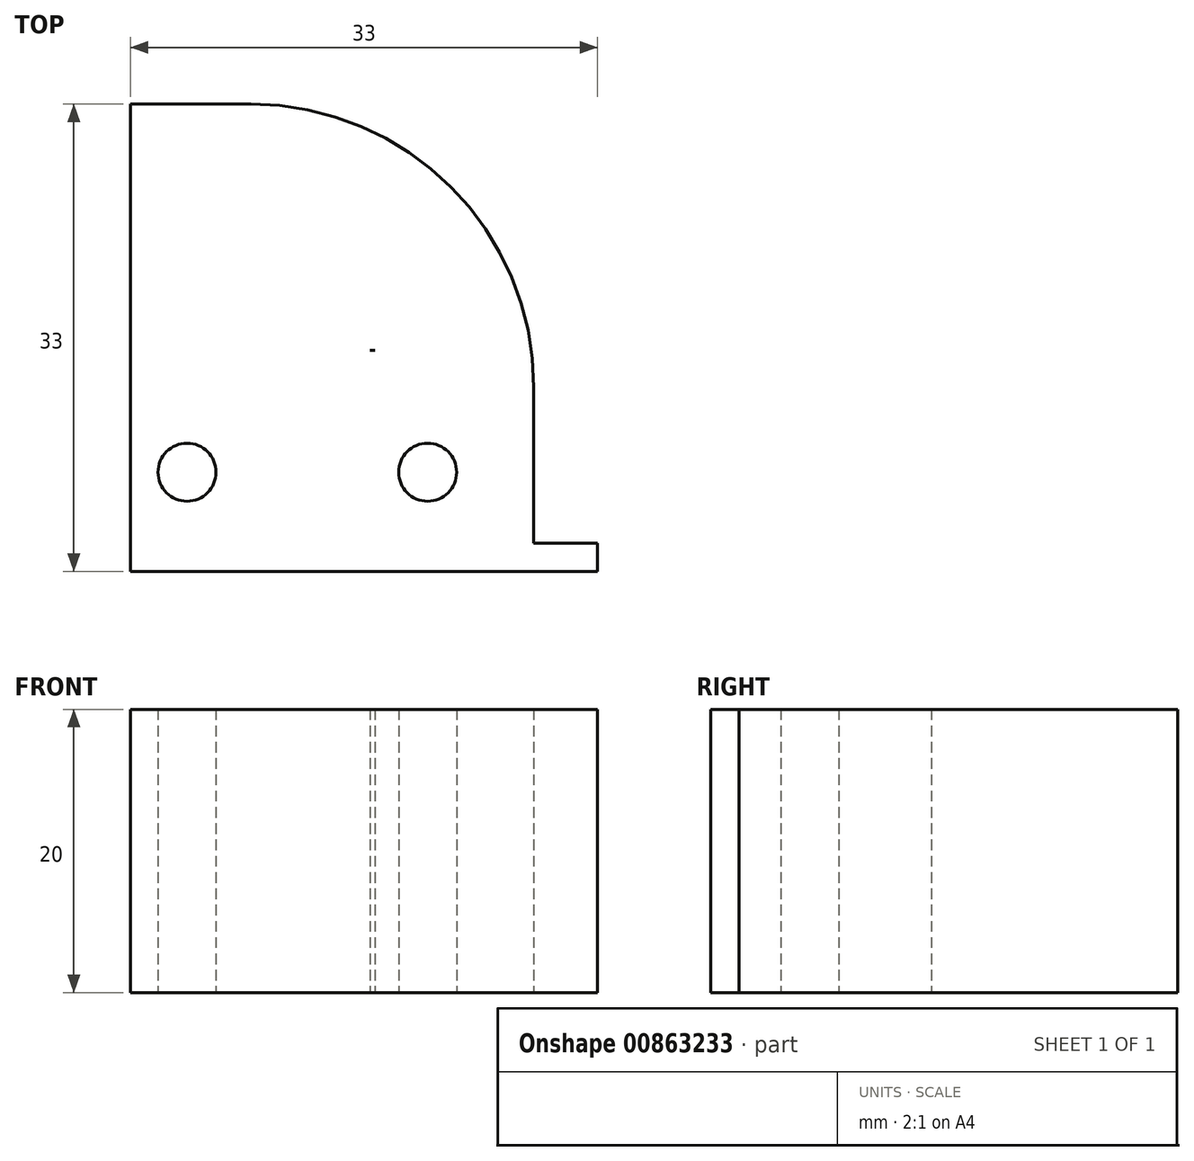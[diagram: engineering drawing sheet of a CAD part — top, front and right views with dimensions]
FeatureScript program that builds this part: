
annotation { "Feature Type Name" : "Feature", "Feature Type Description" : "" }
export const myFeature = defineFeature(function(context is Context, id is Id, definition is map)
    precondition{}
    {
        {
            var Q0;
            Q0=qCreatedBy(makeId("Top.planeOp"),FACE);
            var sketch = newSketch(context, id + "F0", { "sketchPlane" : qUnion([Q0])});
            skLineSegment(sketch, "E0.bottom", {"start": v(0, 0) * mm, "end": v(33, 0) * mm});
            skLineSegment(sketch, "E0.top", {"start": v(0, 33) * mm, "end": v(8.5, 33) * mm});
            skLineSegment(sketch, "E0.left", {"start": v(0, 0) * mm, "end": v(0, 33) * mm});
            skLineSegment(sketch, "E0.right", {"start": v(33, 0) * mm, "end": v(33, 2) * mm});
            skLineSegment(sketch, "E1", {"start": v(33, 2) * mm, "end": v(28.5, 2) * mm});
            skLineSegment(sketch, "E2", {"start": v(28.5, 2) * mm, "end": v(28.5, 13) * mm});
            skArc(sketch, "E3", {"start": v(28.5, 13) * mm, "mid": v(22.64, 27.14) * mm, "end": v(8.5, 33) * mm});
            skCircle(sketch, "E4", {"center": v(4, 7) * mm, "radius": 2.05 * mm});
            skLineSegment(sketch, "E5", {"start": v(4, 7) * mm, "end": v(6.05, 7) * mm});
            skCircle(sketch, "E6", {"center": v(21, 7) * mm, "radius": 2.05 * mm});
            skLineSegment(sketch, "E7.trimOffspring", {"start": v(18.95, 7) * mm, "end": v(21, 7) * mm});
            skArc(sketch, "E8", {"start": v(16.93, 15.6) * mm, "mid": v(23.75, 20.27) * mm, "end": v(21.48, 28.22) * mm});
            skLineSegment(sketch, "E9", {"start": v(17.27, 15.6) * mm, "end": v(-179.81, 15.6) * mm});
            skLineSegment(sketch, "E10", {"start": v(8.5, 33) * mm, "end": v(-178.38, 33) * mm});
            skLineSegment(sketch, "E11", {"start": v(-179.81, 15.6) * mm, "end": v(-179.81, 33) * mm});
            skLineSegment(sketch, "E12", {"start": v(-178.38, 33) * mm, "end": v(-179.81, 33) * mm});
            skSolve(sketch);
        }
        {
            var Q0;
            {var subQ0=sQuery(id+"F0.wireOp",EDGE,"E8");var subQ1=sQuery(id+"F0.wireOp",EDGE,"E3");var subQ2=makeQuery(id+"F0.imprint","INTERSECT",VERTEX,{"disambiguationData":[OD(0.0)],"derivedFrom":[subQ1,subQ0]});Q0=makeQuery(id+"F0.imprint","IMPRINT",FACE,{"disambiguationData":[TD([[makeQuery(id+"F0.imprint","IMPRINT",EDGE,{"disambiguationData":[TD([[subQ2,1.0]])],"derivedFrom":subQ1}),-1.0]])]});}
            var Q1;
            {var subQ7=sQuery(id+"F0.wireOp",EDGE,"E0.bottom");Q1=makeQuery(id+"F0.imprint","IMPRINT",FACE,{"disambiguationData":[TD([[makeQuery(id+"F0.imprint","IMPRINT",EDGE,{"derivedFrom":subQ7}),1.0]])]});}
            var Q2;
            {var subQ0=sQuery(id+"F0.wireOp",EDGE,"E10");var subQ8=sQuery(id+"F0.wireOp",EDGE,"E0.left");var subQ9=makeQuery(id+"F0.imprint","INTERSECT",VERTEX,{"derivedFrom":[subQ8,subQ0]});Q2=makeQuery(id+"F0.imprint","IMPRINT",FACE,{"disambiguationData":[TD([[makeQuery(id+"F0.imprint","IMPRINT",EDGE,{"disambiguationData":[TD([[subQ9,1.0]])],"derivedFrom":subQ8}),-1.0]])]});}
            extrude(context, id + "F1", {"entities" : qUnion([Q0, Q1, Q2]), "depth" : 20 * mm, "offsetDistance" : 25 * mm});
        }
    });
